# Revit family: Haworth_PopUp_Oval
name_source: partatom
category: Furniture
revit_build: Autodesk Revit Architecture 2015 (Build: 20141119_1515(x64)
units: mm (PartAtom-declared; Revit-internal decimal feet)

## types (1)
- 36h 24d 48w
    Actual Depth = 24"
    Actual Height = 36"
    Actual Width = 48"
    Assembly Code = E2020200
    Casters = Yes
    Corner Radius = 6"
    Custom Size = No
    Depth = 24"
    Description = Haworth PopUp - Oval Table - 36h 24d 48w - Casters
    Glides = No
    Leg Height = 34 13/16"
    Manufacturer = Haworth
    Max. Depth = 30"
    Max. Width = 72"
    Min. Depth = 18"
    Min. Width = 48"
    Min/Max Depth = 18, 24, 30in.
    Min/Max Height = 36, 41in.
    Min/Max Width = 48, 54, 60, 66, 72 in.
    Model = TPRP
    Revision Number = 1
    Size = Verify Final Dim. w/ Haworth
    Support Offset = 6"
    Sustainability Info = https://media.haworth.com
    Table 36h = Yes
    Table 41h = No
    Table Thickness = 1 3/16"
    URL = www.haworth.com
    URL - Product = https://www.haworth.com
    Warranty = http://www.haworth.com
    Width = 48"

## geometry (parser evidence)
native form markers: Blend x12, Sweep x6
no freeform markers — native parametric forms only
